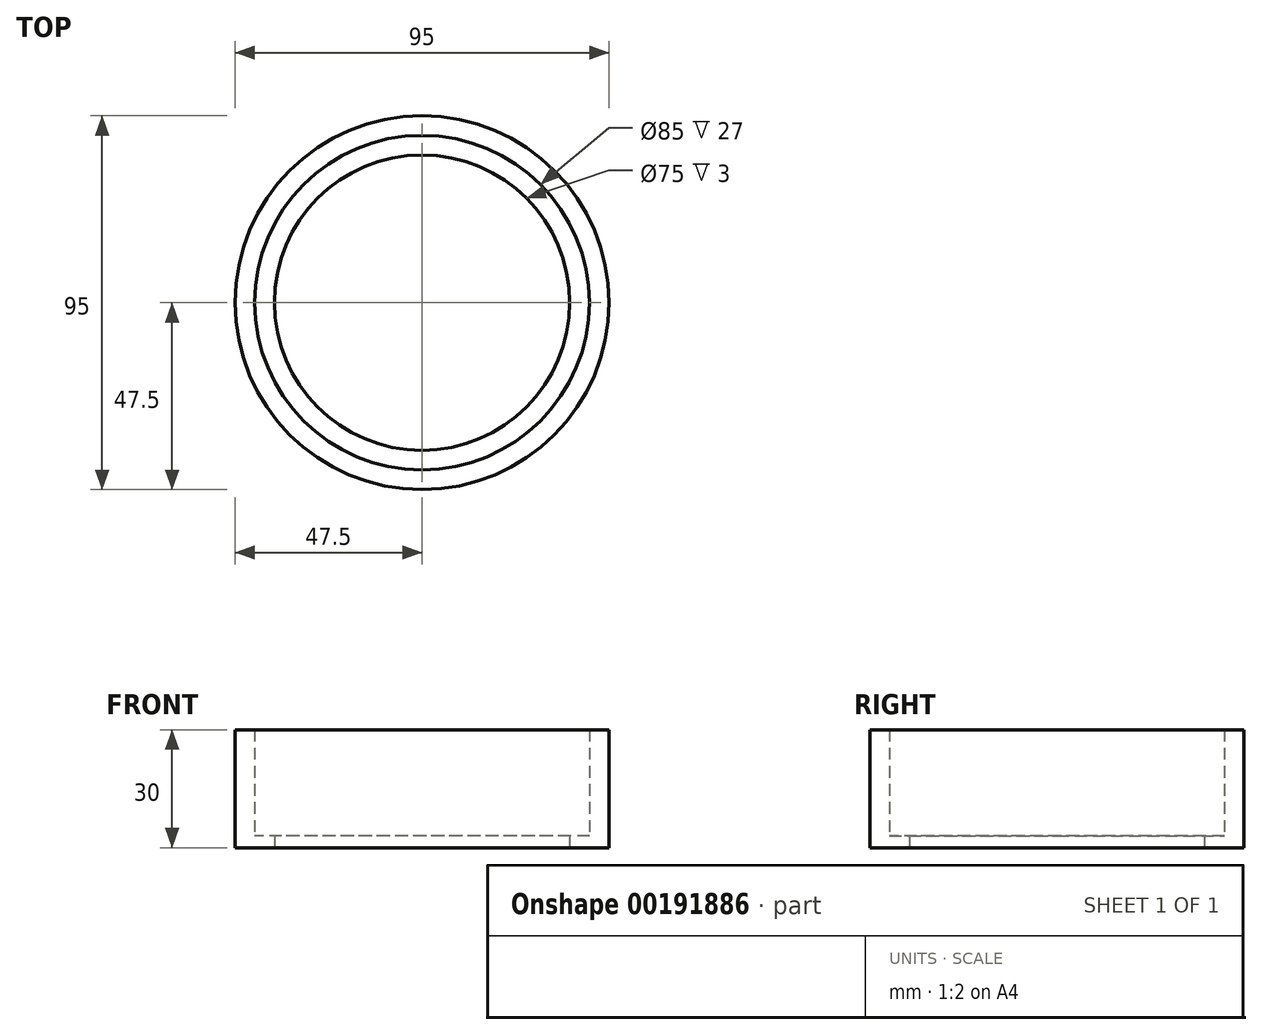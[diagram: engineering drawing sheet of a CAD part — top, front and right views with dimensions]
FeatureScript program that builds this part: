
annotation { "Feature Type Name" : "Feature", "Feature Type Description" : "" }
export const myFeature = defineFeature(function(context is Context, id is Id, definition is map)
    precondition{}
    {
        {
            var Q0;
            Q0=qCreatedBy(makeId("Top.planeOp"),FACE);
            var sketch = newSketch(context, id + "F0", { "sketchPlane" : qUnion([Q0])});
            skCircle(sketch, "E0", {"center": v(0, 0) * mm, "radius": 42.5 * mm});
            skCircle(sketch, "E1.0", {"center": v(0, 0) * mm, "radius": 47.5 * mm});
            skCircle(sketch, "E2", {"center": v(0, 0) * mm, "radius": 37.5 * mm});
            skSolve(sketch);
        }
        {
            var Q0;
            Q0=makeQuery(id+"F0.imprint","IMPRINT",FACE,{"disambiguationData":[TD([[makeQuery(id+"F0.imprint","IMPRINT",EDGE,{"derivedFrom":sQuery(id+"F0.wireOp",EDGE,"E0")}),-1.0]])]});
            extrude(context, id + "F1", {"entities" : qUnion([Q0]), "depth" : 30 * mm});
        }
        {
            var Q0;
            Q0 = qSketchRegion(id + "F0", true);
            var Q1;
            Q1=makeQuery(id+"F0.imprint","IMPRINT",FACE,{"disambiguationData":[TD([[makeQuery(id+"F0.imprint","IMPRINT",EDGE,{"derivedFrom":sQuery(id+"F0.wireOp",EDGE,"E0")}),1.0]])]});
            extrude(context, id + "F2", {"entities" : qUnion([Q0, Q1]), "operationType" : NewBodyOperationType.ADD, "depth" : 3 * mm});
        }
    });
